# Revit family: RN 57070 Optifitt-Press-Inserto di presa con collegamento a pressare
name_source: partatom
category: Rohrformteile
units: mm (PartAtom-declared; Revit-internal decimal feet)

## family parameters
Arbeitsebenenbasiert = Nein
Beim Laden mit Abzugskörper schneiden = Nein
Bemaßung runder Anschluss = Durchmesser verwenden
Gemeinsam genutzt = Nein
Immer vertikal = Ja
Teiletyp = Verbindung

## types (7) — shared parameters
1.010.00.2 Blattnummer der Richtlinie = 29
1.010.00.3 Ausgabedatum (Monat) der Richtlinie = 201308
1.010.00.4 Herstellername = R. Nussbaum AG
1.010.00.5 Revisionsdatum der Datei = 20190521
1.010.00.6 Webadresse des Herstellers = http://www.nussbaum.ch
1.100.00.4 Produktbezeichnung = Versorgung
1.110.00.2 Index = 2
1.110.00.4 Produktbezeichnung = Optifitt-Press
1.960/3L.00.8 Link (URL) = https://www.nussbaum.ch
29.700.00.4 Produktname = Optifitt-Press-Einpressanschluss, für Stahlrohre nach DIN EN 10220/10255
29.700.00.5 Produktkennung = 2
29.700.00.6 Querschnittsform = 1
29.700.00.7 Nennweitensystem = DN
29.700.00.8 Nenndrucksystem = PN
29.710.02.4 Nenndruck = 16
29.710.02.5 max. zul. Überdruck [hPa] = 1600
29.710.02.7 max. zul. Dauer-Betriebsdruck [hPa] = 1600
29.710.02.9 max. zul. Dauer-Betriebstemperatur [°C] = 95
Beschreibung = Optifitt-Press-Inserto di presa con collegamento a pressare
CONNECTOR0_DIAMETER_dX_0r = 20 mm
CONNECTOR0_dX_01 = 15 mm
CONNECTOR0_ref_dX = 15 mm
CONNECTOR1_DIAMETER_dX_0r = 20 mm
CONNECTOR1_dX_00 = 27 mm
CONNECTOR1_dX_01 = 42 mm
CONNECTOR1_ref_dX = 27 mm
Connector Visibility = Nein
EnclosingSpace Visibility = Nein
Hersteller = R. Nussbaum AG
URL = https://www.nussbaum.ch

## per-type parameters (varying)
| type | 1.800.00.3 TGA-Nummer | 1.800.00.4 Kommentarfeld | 1.810.00.3 Hersteller-Bestellnummer | 1.810.00.4 DATANORM-Nummer | 1.810.00.6 GTIN-Nummer | 29.710.02.10 Formstück-Gewicht [kg] | 29.710.02.3 Benennung | Modell | R. Nussbaum AG 57070.27 de Visibility | R. Nussbaum AG 57070.28 de Visibility | R. Nussbaum AG 57070.29 de Visibility | R. Nussbaum AG 57070.30 de Visibility | R. Nussbaum AG 57070.31 de Visibility | R. Nussbaum AG 57070.32 de Visibility | R. Nussbaum AG 57070.33 de Visibility | Typenkommentare |
| DN=100 | 01900200000000000000000000000000000000000000000023???000000000000006 | 57070.33, Optifitt-Press-Einpressanschluss, für Stahlrohre nach DIN EN 10220/10255, DN=100, Rp=¾ | 57070.33 | 57070.33 | 7612945745408 | 0.169 | Optifitt-Press-Einpressanschluss, für Stahlrohre nach DIN EN 10220/10255, DN=100, Rp=¾ | 57070.33 | Nein | Nein | Nein | Nein | Nein | Nein | Ja | Optifitt-Press-Inserto di presa con collegamento a pressare  DN=100 |
| DN=2 | 01900200000000000000000000000000000000000000000023???000000000000005 | 57070.32, Optifitt-Press-Einpressanschluss, für Stahlrohre nach DIN EN 10220/10255, DN=100, Rp=¾ | 57070.32 | 57070.32 | 7612945745392 | 0.172 | Optifitt-Press-Einpressanschluss, für Stahlrohre nach DIN EN 10220/10255, DN=100, Rp=¾ | 57070.32 | Nein | Nein | Nein | Nein | Nein | Ja | Nein | Optifitt-Press-Inserto di presa con collegamento a pressare  DN=100 |
| DN=1 | 01900200000000000000000000000000000000000000000023???000000000000004 | 57070.31, Optifitt-Press-Einpressanschluss, für Stahlrohre nach DIN EN 10220/10255, DN=100, Rp=¾ | 57070.31 | 57070.31 | 7612945745385 | 0.179 | Optifitt-Press-Einpressanschluss, für Stahlrohre nach DIN EN 10220/10255, DN=100, Rp=¾ | 57070.31 | Nein | Nein | Nein | Nein | Ja | Nein | Nein | Optifitt-Press-Inserto di presa con collegamento a pressare  DN=100 |
| DN=80 | 01900200000000000000000000000000000000000000000023???000000000000007 | 57070.30, Optifitt-Press-Einpressanschluss, für Stahlrohre nach DIN EN 10220/10255, DN=80, Rp=¾ | 57070.30 | 57070.30 | 7612945745378 | 0.178 | Optifitt-Press-Einpressanschluss, für Stahlrohre nach DIN EN 10220/10255, DN=80, Rp=¾ | 57070.3 | Nein | Nein | Nein | Ja | Nein | Nein | Nein | Optifitt-Press-Inserto di presa con collegamento a pressare  DN=80 |
| DN=65 | 01900200000000000000000000000000000000000000000023???000000000000003 | 57070.29, Optifitt-Press-Einpressanschluss, für Stahlrohre nach DIN EN 10220/10255, DN=65, Rp=¾ | 57070.29 | 57070.29 | 7612945745361 | 0.179 | Optifitt-Press-Einpressanschluss, für Stahlrohre nach DIN EN 10220/10255, DN=65, Rp=¾ | 57070.29 | Nein | Nein | Ja | Nein | Nein | Nein | Nein | Optifitt-Press-Inserto di presa con collegamento a pressare  DN=65 |
| DN=50 | 01900200000000000000000000000000000000000000000023???000000000000002 | 57070.28, Optifitt-Press-Einpressanschluss, für Stahlrohre nach DIN EN 10220/10255, DN=50, Rp=¾ | 57070.28 | 57070.28 | 7612945745354 | 0.187 | Optifitt-Press-Einpressanschluss, für Stahlrohre nach DIN EN 10220/10255, DN=50, Rp=¾ | 57070.28 | Nein | Ja | Nein | Nein | Nein | Nein | Nein | Optifitt-Press-Inserto di presa con collegamento a pressare  DN=50 |
| DN=40 | 01900200000000000000000000000000000000000000000023???000000000000001 | 57070.27, Optifitt-Press-Einpressanschluss, für Stahlrohre nach DIN EN 10220/10255, DN=40, Rp=¾ | 57070.27 | 57070.27 | 7612945745347 | 0.179 | Optifitt-Press-Einpressanschluss, für Stahlrohre nach DIN EN 10220/10255, DN=40, Rp=¾ | 57070.27 | Ja | Nein | Nein | Nein | Nein | Nein | Nein | Optifitt-Press-Inserto di presa con collegamento a pressare  DN=40 |

## geometry (parser evidence)
native form markers: Sweep x2
no freeform markers — native parametric forms only
